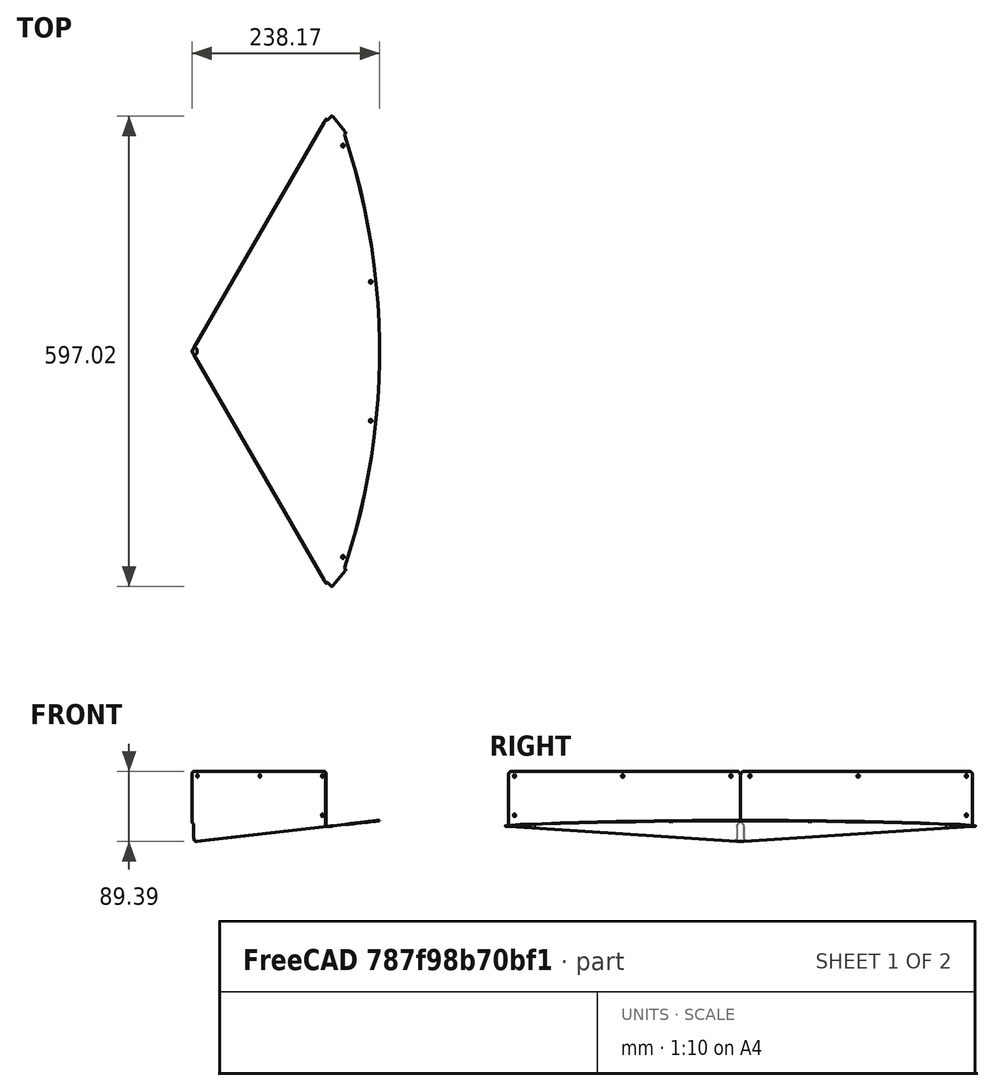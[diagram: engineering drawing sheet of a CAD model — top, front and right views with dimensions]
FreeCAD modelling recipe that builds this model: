
FCSTD DOCUMENT  (FreeCAD 1.1R38827 (Git))
Label: composit_stand3_sink_main
License: All rights reserved
LicenseURL: http://en.wikipedia.org/wiki/All_rights_reserved
objects: Sketcher::SketchObject×8, Part::FeaturePython×4, Part::Mirroring×1, PartDesign::Plane×1, Part::Feature×1, Spreadsheet::Sheet×1
note: 23 computed .brp shape members not serialized (recipe doc carries the construction recipe); baked Part::Feature solids carry a one-line shape summary decoded from their .brp
EXTERNAL_REF file=composit_stand3_main.FCStd obj=Sketch

FEATURE [Sketcher::SketchObject] Sketch001  label="side_bottom_edge"
  ArcFitTolerance = 0
  FullyConstrained = true
  MakeInternals = false
  Placement = pos=(0,0,0) rot=(0.774597,0.447214,0.447214;1.82348rad)
  expr: Constraints[1] = <<composit_stand3_main>>#<<main_sketch>>.Constraints.face_width - 3 mm
  sketch-geometry (1):
    g0: LineSegment StartX=0 StartY=0 StartZ=0 EndX=340.5 EndY=20 EndZ=0
  constraints (5):
    c: Coincident(g-1,g0)
    c: DistanceX(g0) = 340.5
    c: DistanceY(g0) = 20  'y'
    c: Distance(g0) = 341.087  'length'
    c: Angle(g0) = 0.0586697  'angle'
FEATURE [Sketcher::SketchObject] Sketch
  ArcFitTolerance = 0
  ExternalGeometry = -> [Sketch001]
  FullyConstrained = false
  MakeInternals = false
  Placement = pos=(0,0,0) rot=(1,0,0;1.5708rad)
  sketch-geometry (1):
    g0: LineSegment StartX=0 StartY=0 StartZ=0 EndX=141.007 EndY=16.5647 EndZ=0
  constraints (3):
    c: Coincident(g-1,g0)
    c: PointOnObject(g-3,g0)
    c: Angle(g0) = 0.116938  'angle'
FEATURE [Part::Mirroring] Part__Mirroring  label="Sketch001 (Mirror #1)"
  Base = (0,0,0)
  Normal = (0,1,0)
  Source = -> Sketch001
FEATURE [PartDesign::Plane] Plane_1
  AttachmentSupport = -> [Part__Mirroring,Sketch001]
  Length = 66.8539
  MapMode = 13
  Placement = pos=(113.5,-1.89e-14,13.3333) rot=(0.058336,-0.058336,-0.996591;1.57421rad)
  ResizeMode = 0
  Width = 158.88
FEATURE [Sketcher::SketchObject] Sketch003  label="bend_sketch"
  ArcFitTolerance = 0
  AttachmentSupport = -> [Sketch001]
  ExternalGeometry = -> [Sketch]
  FullyConstrained = true
  MakeInternals = false
  MapMode = 7
  Placement = pos=(0,0,0) rot=(0.938382,-0.251439,-0.237103;1.69279rad)
  sketch-geometry (4):
    g0: ArcOfCircle CenterX=2.5 CenterY=2.76676 CenterZ=0 NormalX=0 NormalY=0 NormalZ=1 AngleXU=0 Radius=2.5 StartAngle=3.14159 EndAngle=4.8136
    g1: ArcOfCircle CenterX=2.5 CenterY=2.76676 CenterZ=0 NormalX=0 NormalY=0 NormalZ=1 AngleXU=0 Radius=2 StartAngle=3.14159 EndAngle=4.8136
    g2: LineSegment StartX=2.7526 StartY=0.279556 StartZ=0 EndX=2.70208 EndY=0.776997 EndZ=0
    g3: LineSegment StartX=0 StartY=2.76676 StartZ=0 EndX=0.5 EndY=2.76676 EndZ=0
  constraints (11):
    c: Tangent(g0,g-3) = -1.5708
    c: Tangent(g0,g-2) = 1.5708
    c: Coincident(g1,g0)
    c: Coincident(g2,g0)
    c: Coincident(g2,g1)
    c: Coincident(g3,g0)
    c: Coincident(g3,g1)
    c: Radius(g1) = 2
    c: Perpendicular(g1,g2)
    c: Perpendicular(g1,g3)
    c: Distance(g1,g0) = 0.5
FEATURE [Sketcher::SketchObject] Sketch002  label="edge"
  ArcFitTolerance = 0
  ExternalGeometry = -> [Sketch001,Sketch003]
  FullyConstrained = true
  MakeInternals = false
  Placement = pos=(0,0,0) rot=(0,-1,0;0.116938rad)
  expr: .Placement.Rotation.Angle = <<Sketch>>.Constraints.angle
  sketch-geometry (5):
    g0: ArcOfCircle CenterX=-629.22 CenterY=0 CenterZ=0 NormalX=0 NormalY=0 NormalZ=1 AngleXU=0 Radius=869.22 StartAngle=0 EndAngle=0.322427
    g1: LineSegment [constr] StartX=3.20029 StartY=0 StartZ=0 EndX=173.813 EndY=293.491 EndZ=0
    g2: LineSegment [constr] StartX=171.421 StartY=294.882 StartZ=0 EndX=173.813 EndY=293.491 EndZ=0
    g3: LineSegment StartX=173.813 StartY=293.491 StartZ=0 EndX=195.208 EndY=275.429 EndZ=0
    g4: GeomPoint [constr] X=173.813 Y=293.491 Z=0
  constraints (15):
    c: PointOnObject(g0,g-1)
    c: PointOnObject(g0,g-1)
    c: PointOnObject(g1,g-1)
    c: Parallel(g1,g-3)
    c: Coincident(g2,g-3)
    c: Perpendicular(g2,g1)
    c: Coincident(g1,g2)
    c: PointOnObject(g-4,g1)
    c: DistanceX(g0) = 240
    c: Coincident(g3,g0)
    c: PointOnObject(g4,g3)
    c: PointOnObject(g4,g1)
    c: Coincident(g3,g1)
    c: Angle(g1,g3) = 1.39626
    c: Distance(g3) = 28
FEATURE [Sketcher::SketchObject] Sketch005  label="side_holes_half_sketch"
  ArcFitTolerance = 0
  FullyConstrained = false
  MakeInternals = false
  Placement = pos=(0.433013,-0.25,1e-16) rot=(0.774597,0.447214,0.447214;1.82348rad)
  expr: Placement = <<side_bottom_edge>>.Placement * placement(vector(0; 0; <<Properties>>.thickness); rotation(0; 0; 0))
  sketch-geometry (6):
    g0: Circle CenterX=14.3756 CenterY=84 CenterZ=0 NormalX=0 NormalY=0 NormalZ=1 AngleXU=0 Radius=1.7
    g1: Circle CenterX=173.002 CenterY=84 CenterZ=0 NormalX=0 NormalY=0 NormalZ=1 AngleXU=0 Radius=1.7
    g2: Circle CenterX=331.628 CenterY=84 CenterZ=0 NormalX=0 NormalY=0 NormalZ=1 AngleXU=0 Radius=1.7
    g3: LineSegment [constr] StartX=14.3756 StartY=84 StartZ=0 EndX=173.002 EndY=84 EndZ=0
    g4: LineSegment [constr] StartX=173.002 StartY=84 StartZ=0 EndX=331.628 EndY=84 EndZ=0
    g5: Circle CenterX=331.628 CenterY=34 CenterZ=0 NormalX=0 NormalY=0 NormalZ=1 AngleXU=0 Radius=1.7
  constraints (15):
    c: Coincident(g3,g0)
    c: Coincident(g3,g1)
    c: Coincident(g4,g1)
    c: Coincident(g4,g2)
    c: Equal(g0,g1)
    c: Equal(g1,g2)
    c: Equal(g3,g4)
    c: DistanceY(g0) = 84
    c: DistanceX(g0,g2) = 317.253
    c: DistanceY(g5,g2) = 50
    c: DistanceX(g0) = 14.3756
    c: Horizontal(g3)
    c: Horizontal(g4)
    c: Diameter(g0) = 3.4
    c: Equal(g5,g0)
FEATURE [Part::FeaturePython] Downgrade  label="Wires of Sketch005"  # WARN: FeaturePython — macro-defined, semantics opaque (R4)
  Base = -> Sketch005
  Mode = 7
FEATURE [Part::FeaturePython] ArrayFromShape  label="side_holes_half"  # WARN: FeaturePython — macro-defined, semantics opaque (R4)
  CompoundTraversal = 1
  ExposePlacement = false
  MarkerShape = 1
  MarkerSize = 50
  NumElements = 4
  OrientElementIndex = 0
  OrientMode = 2
  ShapeLink = -> Downgrade
  TranslateElementIndex = 0
  TranslateMode = 3
  Type = lattice2ArrayFromShape.LatticeArrayFromShape
  isLattice = 1
FEATURE [Part::FeaturePython] Mirror  label="Mirror of Array from Wires of Sketch005"  # WARN: FeaturePython — macro-defined, semantics opaque (R4)
  ExposePlacement = false
  FlipX = false
  FlipY = true
  FlipZ = false
  MarkerShape = 1
  MarkerSize = 0
  NumElements = 4
  Object = -> ArrayFromShape
  ObjectTraversal = 0
  Type = lattice2Mirror.LatticeMirror
  isLattice = 1
FEATURE [Part::FeaturePython] Join  label="holes_placements"  # WARN: FeaturePython — macro-defined, semantics opaque (R4)
  ExposePlacement = false
  Interleave = false
  Links = -> [ArrayFromShape,Mirror]
  MarkerShape = 1
  MarkerSize = 0
  NumElements = 8
  Type = lattice2JoinArrays.JoinArrays
  isLattice = 1
FEATURE [Part::Feature] Body158  label="sink_material_0.30ansi002"
  Placement = pos=(0,0,0) rot=(0,0,-1;1.5708rad)
  shape: bbox 238.2 x 597 x 89.39 mm, 56 faces (baked)
FEATURE [Sketcher::SketchObject] Sketch006  label="side_intersection"
  ArcFitTolerance = 1e-06
  FullyConstrained = true
  MakeInternals = false
  expr: Constraints[7] = <<Properties>>.thickness
  sketch-geometry (3):
    g0: LineSegment StartX=0 StartY=0 StartZ=0 EndX=0.202073 EndY=0.35 EndZ=0
    g1: LineSegment StartX=0.202073 StartY=0.35 StartZ=0 EndX=0.635085 EndY=0.1 EndZ=0
    g2: LineSegment StartX=0.635085 StartY=0.1 StartZ=0 EndX=0.635085 EndY=0 EndZ=0
  constraints (10):
    c: Coincident(g-1,g0)
    c: Coincident(g0,g1)
    c: Coincident(g1,g2)
    c: PointOnObject(g2,g-1)
    c: Vertical(g2)
    c: Angle(g0) = 1.0472
    c: Perpendicular(g0,g1)
    c: Distance(g1) = 0.5
    c: DistanceY(g2,g2) = 0.1
    c: Distance(g0) = 0.404145  'offset'
FEATURE [Sketcher::SketchObject] Sketch004  label="side_sketch"
  ArcFitTolerance = 0
  ExternalGeometry = -> [Sketch001,Sketch003,Sketch006]
  FullyConstrained = true
  MakeInternals = false
  Placement = pos=(0,0,0) rot=(0.774597,0.447214,0.447214;1.82348rad)
  sketch-geometry (6):
    g0: LineSegment StartX=0.404145 StartY=2.79527 StartZ=0 EndX=0.404145 EndY=90 EndZ=0
    g1: LineSegment StartX=0.404145 StartY=90 StartZ=0 EndX=340.338 EndY=90 EndZ=0
    g2: LineSegment StartX=340.338 StartY=90 StartZ=0 EndX=340.338 EndY=22.762 EndZ=0
    g3: LineSegment StartX=340.338 StartY=22.762 StartZ=0 EndX=0.404145 EndY=2.79527 EndZ=0
    g4: LineSegment [constr] StartX=0 StartY=0 StartZ=0 EndX=-0.162232 EndY=2.762 EndZ=0
    g5: LineSegment [constr] StartX=340.5 StartY=20 StartZ=0 EndX=340.338 EndY=22.762 EndZ=0
  constraints (16):
    c: Vertical(g0)
    c: Coincident(g0,g1)
    c: Coincident(g1,g2)
    c: Coincident(g2,g3)
    c: Coincident(g3,g0)
    c: Parallel(g3,g-3)
    c: PointOnObject(g-4,g3)
    c: Horizontal(g1)
    c: Vertical(g2)
    c: DistanceY(g0) = 90
    c: Vertical(g-5,g0)
    c: Coincident(g4,g-1)
    c: Coincident(g4,g-4)
    c: Coincident(g5,g-3)
    c: Coincident(g5,g2)
    c: Parallel(g5,g4)
FEATURE [Spreadsheet::Sheet] Spreadsheet  label="Properties"
  cells = B2(thickness)==0.5 mm
FEATURE [Sketcher::SketchObject] Sketch007
  ArcFitTolerance = 1e-06
  ExternalGeometry = -> [Sketch002]
  FullyConstrained = true
  MakeInternals = false
  Placement = pos=(0,0,0) rot=(0,-1,0;0.116938rad)
  expr: Placement = <<edge>>.Placement
  sketch-geometry (8):
    g0: LineSegment StartX=195.208 StartY=275.429 StartZ=0 EndX=196.102 EndY=276.487 EndZ=0
    g1: LineSegment StartX=196.109 StartY=279.059 StartZ=0 EndX=180.5 EndY=297.774 EndZ=0
    g2: LineSegment StartX=177.436 StartY=297.783 StartZ=0 EndX=173.813 EndY=293.491 EndZ=0
    g3: ArcOfCircle CenterX=194.573 CenterY=277.778 CenterZ=0 NormalX=0 NormalY=0 NormalZ=1 AngleXU=0 Radius=2 StartAngle=5.58208 EndAngle=6.97834
    g4: GeomPoint [constr] X=197.184 Y=277.77 Z=0
    g5: ArcOfCircle CenterX=178.964 CenterY=296.493 CenterZ=0 NormalX=0 NormalY=0 NormalZ=1 AngleXU=0 Radius=2 StartAngle=0.695159 EndAngle=2.44049
    g6: GeomPoint [constr] X=178.973 Y=299.604 Z=0
    g7: LineSegment StartX=173.813 StartY=293.491 StartZ=0 EndX=195.208 EndY=275.429 EndZ=0
  constraints (18):
    c: Coincident(g-3,g0)
    c: Coincident(g2,g-3)
    c: Perpendicular(g-3,g0)
    c: Perpendicular(g-3,g2)
    c: Distance(g2,g6) = 8
    c: PointOnObject(g4,g0)
    c: PointOnObject(g4,g1)
    c: Tangent(g0,g3) = -1.5708
    c: Tangent(g1,g3) = -1.5708
    c: PointOnObject(g6,g1)
    c: PointOnObject(g6,g2)
    c: Tangent(g1,g5) = -1.5708
    c: Tangent(g2,g5) = -1.5708
    c: Angle(g2,g1) = 1.39626
    c: Equal(g5,g3)
    c: Radius(g5) = 2
    c: Coincident(g7,g2)
    c: Coincident(g7,g0)
